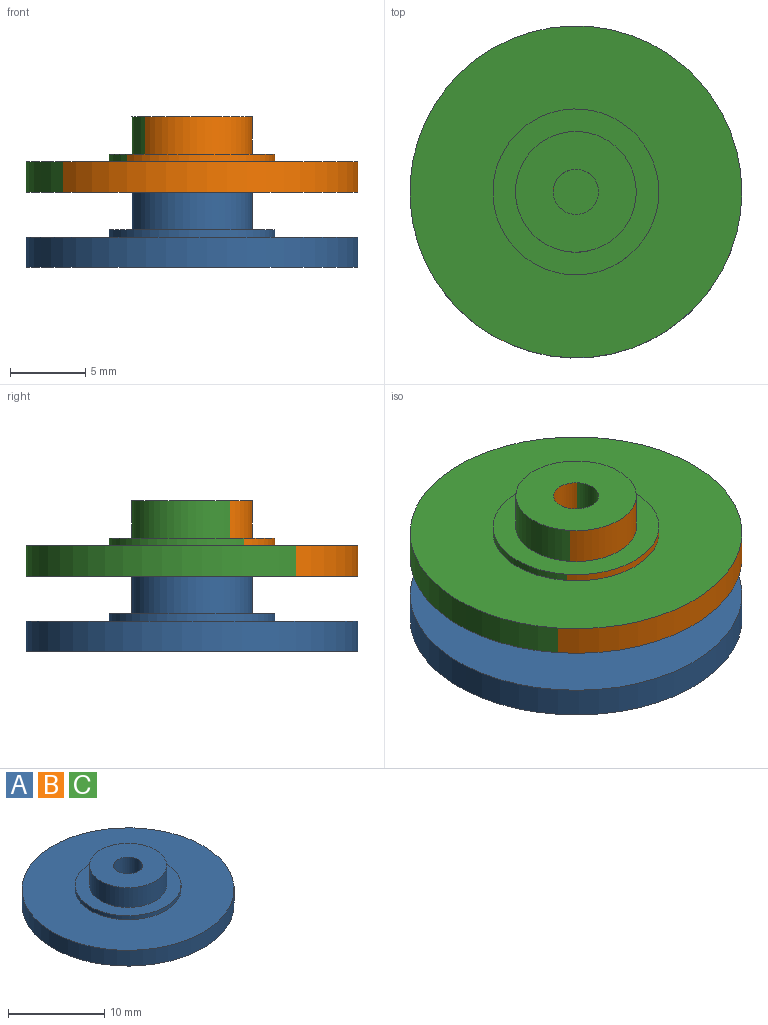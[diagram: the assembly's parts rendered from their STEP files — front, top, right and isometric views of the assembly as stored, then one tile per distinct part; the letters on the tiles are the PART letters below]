
ASSEMBLY  parts=3 mates=1
PART A: 28 faces, bbox 22x22x5 mm
  f0: plane 22x22mm, normal (0,0,-1), area 362.2mm2, adj f6,f9,f10,f11,f12,f14,f15,f16
  f1: cylinder r=1.5mm len=4mm, axis (0,0,-1), area 37.7mm2, adj f3,f8
  f2: cylinder r=4mm len=8mm, axis (0,0,-1), area 62.8mm2, adj f3,f5
  f3: plane 8x8mm, normal (0,0,1), area 43.2mm2, adj f1,f2
  f4: cylinder r=5.5mm len=11mm, axis (0,0,-1), area 17.3mm2, adj f5,f7
  f5: plane 11x11mm, normal (0,0,1), area 44.8mm2, adj f2,f4
  f6: cylinder r=11mm len=22mm, axis (0,0,-1), area 138.2mm2, adj f0,f7
  f7: plane 22x22mm, normal (0,0,1), area 285.1mm2, adj f4,f6
  f8: plane 3x3mm, normal (0,0,1), area 7.1mm2, adj f1
  f9: plane 0.82x0.77mm, normal (-0.73,0.68,0), area 0.8mm2, adj f0,f10,f12,f13
  f10: plane 7.23x0.78mm, normal (0.11,0.99,0), area 5.5mm2, adj f0,f9,f11,f13
  f11: plane 1.49x0.75mm, normal (0.91,0.41,0), area 1.2mm2, adj f0,f10,f12,f13
  f12: plane 8.66x1.44mm, normal (-0.16,-0.99,0), area 6.6mm2, adj f0,f9,f11,f13
  f13: plane 8.66x2.26mm, normal (0,0,-1), area 9.2mm2, adj f9,f10,f11,f12
  f14: plane 2.51x0.75mm, normal (0.1,1,0), area 1.9mm2, adj f0,f15,f17,f18
  f15: plane 1.17x0.75mm, normal (0.91,0.41,0), area 1mm2, adj f0,f14,f16,f18
  f16: plane 3.55x0.85mm, normal (-0.23,-0.97,0), area 2.7mm2, adj f0,f15,f17,f18
  f17: plane 0.75x0.56mm, normal (-0.73,0.68,0), area 0.6mm2, adj f0,f14,f16,f18
  f18: plane 3.55x1.41mm, normal (0,0,-1), area 2.6mm2, adj f14,f15,f16,f17
  f19: plane 4.81x0.75mm, normal (0.09,1,0), area 3.6mm2, adj f0,f20,f22,f23
  f20: plane 1.35x0.75mm, normal (0.91,0.41,0), area 1.1mm2, adj f0,f19,f21,f23
  f21: plane 5.98x1.17mm, normal (-0.19,-0.98,0), area 4.6mm2, adj f0,f20,f22,f23
  f22: plane 0.75x0.61mm, normal (-0.73,0.68,0), area 0.6mm2, adj f0,f19,f21,f23
  f23: plane 5.98x1.78mm, normal (0,0,-1), area 5.3mm2, adj f19,f20,f21,f22
  f24: plane 1.4x0.75mm, normal (0.91,0.41,0), area 1.1mm2, adj f0,f25,f26,f27
  f25: plane 1.45x0.75mm, normal (-0.33,-0.95,0), area 1.2mm2, adj f0,f24,f26,f27
  f26: plane 0.9x0.83mm, normal (-0.73,0.68,0), area 0.9mm2, adj f0,f24,f25,f27
  f27: plane 1.45x1.4mm, normal (0,0,-1), area 0.9mm2, adj f24,f25,f26
PART B: same geometry as A
PART C: same geometry as A
PLACE A t=(31.14,-43.31,36.39)mm
PLACE B t=(31.14,-43.31,41.39)mm
PLACE C t=(31.14,-43.31,41.39)mm
MATE planar A.f1 <-> C.f1  axis (0,0,1) through (-28.35,8.88,41.39)mm
